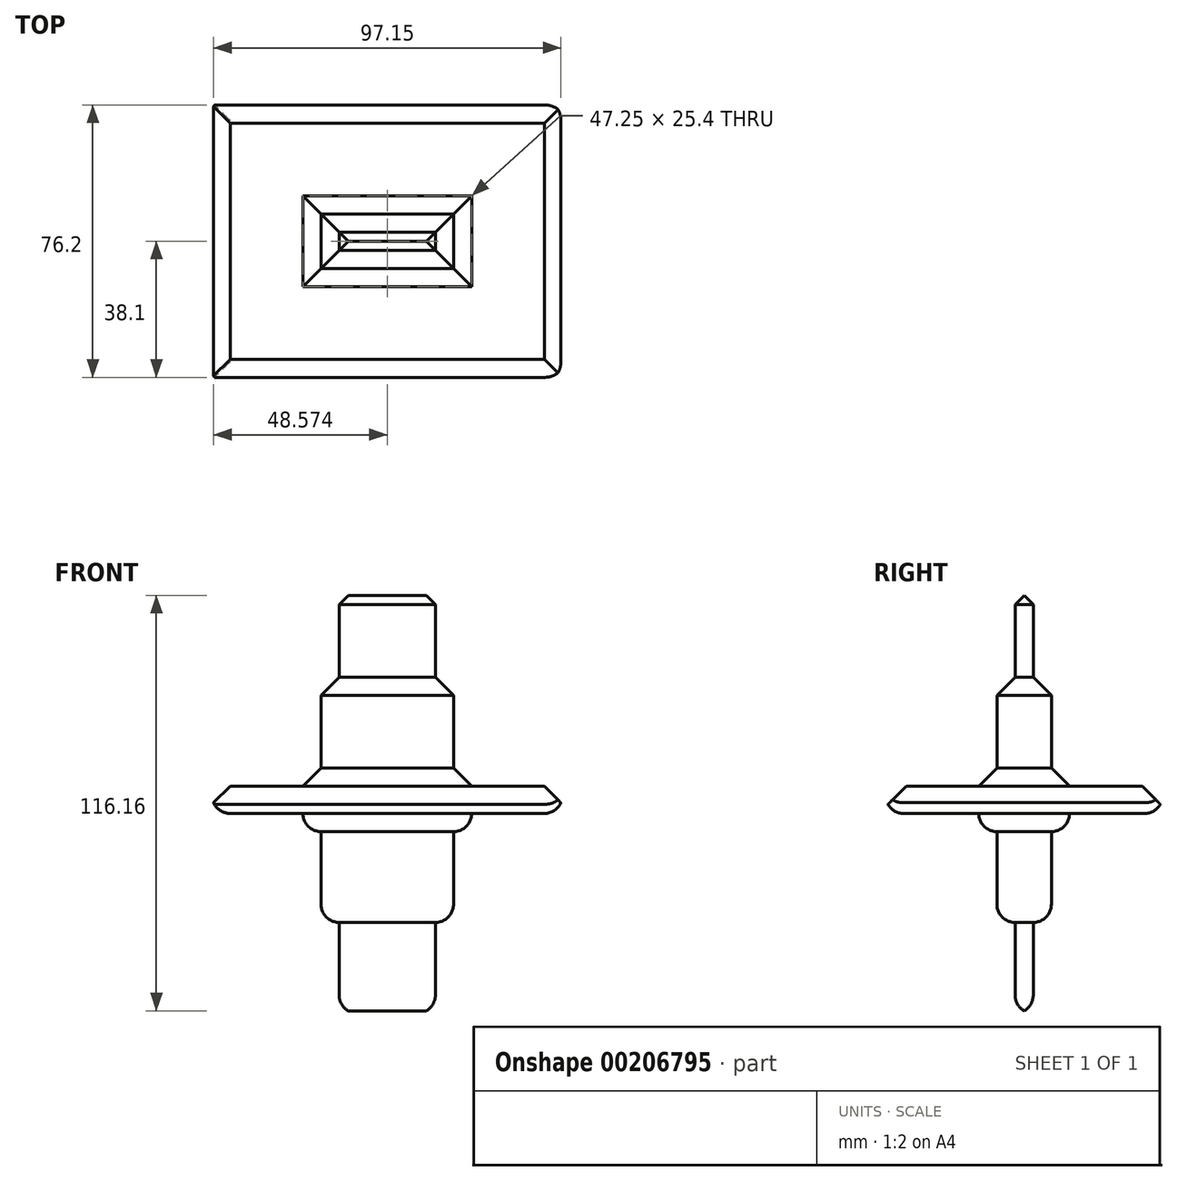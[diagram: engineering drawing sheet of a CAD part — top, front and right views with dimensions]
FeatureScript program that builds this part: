
annotation { "Feature Type Name" : "Feature", "Feature Type Description" : "" }
export const myFeature = defineFeature(function(context is Context, id is Id, definition is map)
    precondition{}
    {
        {
            var Q0;
            Q0=qCreatedBy(makeId("Front.planeOp"),FACE);
            var sketch = newSketch(context, id + "F0", { "sketchPlane" : qUnion([Q0])});
            skLineSegment(sketch, "E0", {"start": v(27.15, 7.6) * mm, "end": v(27.15, -10.17) * mm});
            skLineSegment(sketch, "E1", {"start": v(27.15, -10.17) * mm, "end": v(-20.1, -10.17) * mm});
            skLineSegment(sketch, "E2", {"start": v(-20.1, -10.17) * mm, "end": v(-20.1, 7.6) * mm});
            skLineSegment(sketch, "E3", {"start": v(-20.1, 7.6) * mm, "end": v(27.15, 7.6) * mm});
            skSolve(sketch);
        }
        {
            var Q0;
            Q0 = qSketchRegion(id + "F0", true);
            extrude(context, id + "F1", {"entities" : qUnion([Q0]), "depth" : 25.4 * mm});
        }
        {
            var Q0;
            Q0=makeQuery(id+"F1.opExtrude","SWEPT_FACE",FACE,{"disambiguationData":[OSD([sQuery(id+"F0.wireOp",EDGE,"E3")])]});
            chamfer(context, id + "F2", {"entities" : qUnion([Q0]), "width" : 5.08 * mm, "tangentPropagation" : true});
        }
        {
            var Q0;
            Q0=makeQuery(id+"F1.opExtrude","SWEPT_FACE",FACE,{"disambiguationData":[OSD([sQuery(id+"F0.wireOp",EDGE,"E1")])]});
            fillet(context, id + "F3", {"entities" : qUnion([Q0]), "radius" : 5.08 * mm, "tangentPropagation" : true, "allowEdgeOverflow" : false});
        }
        {
            var Q0;
            Q0=makeQuery(id+"F1.opExtrude","SWEPT_FACE",FACE,{"disambiguationData":[OSD([sQuery(id+"F0.wireOp",EDGE,"E1")])]});
            extrude(context, id + "F4", {"entities" : qUnion([Q0]), "operationType" : NewBodyOperationType.ADD, "depth" : 25.4 * mm});
        }
        {
            var Q0;
            Q0=makeQuery(id+"F4.opExtrude","CAP_FACE",FACE,{"disambiguationData":[OSD([sQuery(id+"F0.wireOp",EDGE,"E1")])],"isStart":false});
            fillet(context, id + "F5", {"entities" : qUnion([Q0]), "radius" : 5.08 * mm, "tangentPropagation" : true, "allowEdgeOverflow" : false});
        }
        {
            var Q0;
            Q0=makeQuery(id+"F4.opExtrude","CAP_FACE",FACE,{"disambiguationData":[OSD([sQuery(id+"F0.wireOp",EDGE,"E1")])],"isStart":false});
            extrude(context, id + "F6", {"entities" : qUnion([Q0]), "operationType" : NewBodyOperationType.ADD, "depth" : 25.4 * mm});
        }
        {
            var Q0;
            Q0=makeQuery(id+"F6.opExtrude","CAP_FACE",FACE,{"disambiguationData":[OSD([sQuery(id+"F0.wireOp",EDGE,"E1")])],"isStart":false});
            fillet(context, id + "F7", {"entities" : qUnion([Q0]), "radius" : 5.08 * mm, "tangentPropagation" : true, "allowEdgeOverflow" : false});
        }
        {
            var Q0;
            Q0=makeQuery(id+"F1.opExtrude","SWEPT_FACE",FACE,{"disambiguationData":[OSD([sQuery(id+"F0.wireOp",EDGE,"E3")])]});
            extrude(context, id + "F8", {"entities" : qUnion([Q0]), "operationType" : NewBodyOperationType.ADD, "depth" : 25.4 * mm});
        }
        {
            var Q0;
            Q0=makeQuery(id+"F8.opExtrude","CAP_FACE",FACE,{"disambiguationData":[OSD([sQuery(id+"F0.wireOp",EDGE,"E3")])],"isStart":false});
            chamfer(context, id + "F9", {"entities" : qUnion([Q0]), "width" : 5.08 * mm, "tangentPropagation" : true});
        }
        {
            var Q0;
            Q0=makeQuery(id+"F8.opExtrude","CAP_FACE",FACE,{"disambiguationData":[OSD([sQuery(id+"F0.wireOp",EDGE,"E3")])],"isStart":false});
            extrude(context, id + "F10", {"entities" : qUnion([Q0]), "operationType" : NewBodyOperationType.ADD, "depth" : 25.4 * mm});
        }
        {
            var Q0;
            Q0=makeQuery(id+"F10.opExtrude","CAP_FACE",FACE,{"disambiguationData":[OSD([sQuery(id+"F0.wireOp",EDGE,"E3")])],"isStart":false});
            chamfer(context, id + "F11", {"entities" : qUnion([Q0]), "width" : 5.08 * mm, "tangentPropagation" : true});
        }
        {
            var Q0;
            Q0=makeQuery(id+"F1.opExtrude","CAP_FACE",FACE,{"disambiguationData":[OSD([sQuery(id+"F0.wireOp",EDGE,"E0"),sQuery(id+"F0.wireOp",EDGE,"E1"),sQuery(id+"F0.wireOp",EDGE,"E2"),sQuery(id+"F0.wireOp",EDGE,"E3")])],"isStart":true});
            extrude(context, id + "F12", {"entities" : qUnion([Q0]), "operationType" : NewBodyOperationType.ADD, "depth" : 25.4 * mm});
        }
        {
            var Q0;
            {var subQ0=sQuery(id+"F0.wireOp",EDGE,"E3");var subQ1=sQuery(id+"F0.wireOp",EDGE,"E2");var subQ2=sQuery(id+"F0.wireOp",EDGE,"E1");var subQ3=sQuery(id+"F0.wireOp",EDGE,"E0");Q0=makeQuery(id+"F12.opExtrude","CAP_EDGE",EDGE,{"disambiguationData":[OSD([subQ3,subQ2,subQ1,subQ0]),TDD([makeQuery(id+"F2.opChamfer","BLEND_EDGE",EDGE,{"blendedFrom":[makeQuery(id+"F1.opExtrude","CAP_EDGE",EDGE,{"disambiguationData":[OSD([subQ0])],"isStart":true}),makeQuery(id+"F1.opExtrude","CAP_FACE",FACE,{"disambiguationData":[OSD([subQ3,subQ2,subQ1,subQ0])],"isStart":true})],"blendedInto":[makeQuery(id+"F1.opExtrude","CAP_FACE",FACE,{"disambiguationData":[OSD([subQ3,subQ2,subQ1,subQ0])],"isStart":true})]})])],"isStart":false});}
            chamfer(context, id + "F13", {"entities" : qUnion([Q0]), "width" : 5.08 * mm, "tangentPropagation" : true});
        }
        {
            var Q0;
            {var subQ0=sQuery(id+"F0.wireOp",EDGE,"E3");var subQ1=sQuery(id+"F0.wireOp",EDGE,"E2");var subQ2=sQuery(id+"F0.wireOp",EDGE,"E1");var subQ3=sQuery(id+"F0.wireOp",EDGE,"E0");Q0=makeQuery(id+"F12.opExtrude","CAP_EDGE",EDGE,{"disambiguationData":[OSD([subQ3,subQ2,subQ1,subQ0]),TDD([makeQuery(id+"F3.opFillet","BLEND_EDGE",EDGE,{"blendedFrom":[makeQuery(id+"F1.opExtrude","CAP_EDGE",EDGE,{"disambiguationData":[OSD([subQ2])],"isStart":true}),makeQuery(id+"F1.opExtrude","CAP_FACE",FACE,{"disambiguationData":[OSD([subQ3,subQ2,subQ1,subQ0])],"isStart":true})],"blendedInto":[makeQuery(id+"F1.opExtrude","CAP_FACE",FACE,{"disambiguationData":[OSD([subQ3,subQ2,subQ1,subQ0])],"isStart":true})]})])],"isStart":false});}
            fillet(context, id + "F14", {"entities" : qUnion([Q0]), "radius" : 5.08 * mm, "tangentPropagation" : true, "allowEdgeOverflow" : false});
        }
        {
            var Q0;
            Q0=makeQuery(id+"F1.opExtrude","CAP_FACE",FACE,{"disambiguationData":[OSD([sQuery(id+"F0.wireOp",EDGE,"E0"),sQuery(id+"F0.wireOp",EDGE,"E1"),sQuery(id+"F0.wireOp",EDGE,"E2"),sQuery(id+"F0.wireOp",EDGE,"E3")])],"isStart":false});
            extrude(context, id + "F15", {"entities" : qUnion([Q0]), "operationType" : NewBodyOperationType.ADD, "depth" : 25.4 * mm});
        }
        {
            var Q0;
            {var subQ0=sQuery(id+"F0.wireOp",EDGE,"E3");var subQ1=sQuery(id+"F0.wireOp",EDGE,"E2");var subQ2=sQuery(id+"F0.wireOp",EDGE,"E1");var subQ3=sQuery(id+"F0.wireOp",EDGE,"E0");Q0=makeQuery(id+"F15.opExtrude","CAP_EDGE",EDGE,{"disambiguationData":[OSD([subQ3,subQ2,subQ1,subQ0]),TDD([makeQuery(id+"F2.opChamfer","BLEND_EDGE",EDGE,{"blendedFrom":[makeQuery(id+"F1.opExtrude","CAP_EDGE",EDGE,{"disambiguationData":[OSD([subQ0])],"isStart":false}),makeQuery(id+"F1.opExtrude","CAP_FACE",FACE,{"disambiguationData":[OSD([subQ3,subQ2,subQ1,subQ0])],"isStart":false})],"blendedInto":[makeQuery(id+"F1.opExtrude","CAP_FACE",FACE,{"disambiguationData":[OSD([subQ3,subQ2,subQ1,subQ0])],"isStart":false})]})])],"isStart":false});}
            chamfer(context, id + "F16", {"entities" : qUnion([Q0]), "width" : 5.08 * mm, "tangentPropagation" : true});
        }
        {
            var Q0;
            {var subQ0=sQuery(id+"F0.wireOp",EDGE,"E3");var subQ1=sQuery(id+"F0.wireOp",EDGE,"E2");var subQ2=sQuery(id+"F0.wireOp",EDGE,"E1");var subQ3=sQuery(id+"F0.wireOp",EDGE,"E0");Q0=makeQuery(id+"F15.opExtrude","CAP_EDGE",EDGE,{"disambiguationData":[OSD([subQ3,subQ2,subQ1,subQ0]),TDD([makeQuery(id+"F3.opFillet","BLEND_EDGE",EDGE,{"blendedFrom":[makeQuery(id+"F1.opExtrude","CAP_EDGE",EDGE,{"disambiguationData":[OSD([subQ2])],"isStart":false}),makeQuery(id+"F1.opExtrude","CAP_FACE",FACE,{"disambiguationData":[OSD([subQ3,subQ2,subQ1,subQ0])],"isStart":false})],"blendedInto":[makeQuery(id+"F1.opExtrude","CAP_FACE",FACE,{"disambiguationData":[OSD([subQ3,subQ2,subQ1,subQ0])],"isStart":false})]})])],"isStart":false});}
            fillet(context, id + "F17", {"entities" : qUnion([Q0]), "radius" : 5.08 * mm, "tangentPropagation" : true, "allowEdgeOverflow" : false});
        }
        {
            var Q0;
            {var subQ0=sQuery(id+"F0.wireOp",EDGE,"E2");Q0=makeQuery(id+"F15.boolean.opBoolean","MERGE",FACE,{"derivedFrom":[makeQuery(id+"F12.boolean.opBoolean","MERGE",FACE,{"derivedFrom":[makeQuery(id+"F1.opExtrude","SWEPT_FACE",FACE,{"disambiguationData":[OSD([subQ0])]}),makeQuery(id+"F12.opExtrude","SWEPT_FACE",FACE,{"disambiguationData":[OSD([subQ0])]})]}),makeQuery(id+"F15.opExtrude","SWEPT_FACE",FACE,{"disambiguationData":[OSD([subQ0])]})]});}
            extrude(context, id + "F18", {"entities" : qUnion([Q0]), "operationType" : NewBodyOperationType.ADD, "depth" : 25.4 * mm});
        }
        {
            var Q0;
            {var subQ0=sQuery(id+"F0.wireOp",EDGE,"E2");var subQ1=makeQuery(id+"F1.opExtrude","SWEPT_FACE",FACE,{"disambiguationData":[OSD([subQ0])]});var subQ2=sQuery(id+"F0.wireOp",EDGE,"E3");var subQ3=sQuery(id+"F0.wireOp",EDGE,"E1");var subQ4=sQuery(id+"F0.wireOp",EDGE,"E0");var subQ5=makeQuery(id+"F1.opExtrude","SWEPT_EDGE",EDGE,{"disambiguationData":[OSD([subQ3,subQ0])]});Q0=makeQuery(id+"F18.opExtrude","CAP_EDGE",EDGE,{"disambiguationData":[OSD([subQ4,subQ3,subQ0,subQ2]),TDD([makeQuery(id+"F3.opFillet","BLEND_EDGE",EDGE,{"blendedFrom":[subQ5,subQ1],"blendedInto":[subQ1]}),makeQuery(id+"F12.opExtrude","SWEPT_EDGE",EDGE,{"disambiguationData":[OSD([subQ4,subQ3,subQ0,subQ2]),TDD([makeQuery(id+"F3.opFillet","BLEND_VERTEX",VERTEX,{"blendedFrom":[subQ5,makeQuery(id+"F1.opExtrude","CAP_EDGE",EDGE,{"disambiguationData":[OSD([subQ3])],"isStart":true}),makeQuery(id+"F1.opExtrude","CAP_FACE",FACE,{"disambiguationData":[OSD([subQ4,subQ3,subQ0,subQ2])],"isStart":true}),subQ1],"blendedInto":[makeQuery(id+"F1.opExtrude","CAP_FACE",FACE,{"disambiguationData":[OSD([subQ4,subQ3,subQ0,subQ2])],"isStart":true}),subQ1]})])]}),makeQuery(id+"F15.opExtrude","SWEPT_EDGE",EDGE,{"disambiguationData":[OSD([subQ4,subQ3,subQ0,subQ2]),TDD([makeQuery(id+"F3.opFillet","BLEND_VERTEX",VERTEX,{"blendedFrom":[subQ5,makeQuery(id+"F1.opExtrude","CAP_EDGE",EDGE,{"disambiguationData":[OSD([subQ3])],"isStart":false}),makeQuery(id+"F1.opExtrude","CAP_FACE",FACE,{"disambiguationData":[OSD([subQ4,subQ3,subQ0,subQ2])],"isStart":false}),subQ1],"blendedInto":[makeQuery(id+"F1.opExtrude","CAP_FACE",FACE,{"disambiguationData":[OSD([subQ4,subQ3,subQ0,subQ2])],"isStart":false}),subQ1]})])]})])],"isStart":false});}
            fillet(context, id + "F19", {"entities" : qUnion([Q0]), "radius" : 5.08 * mm, "tangentPropagation" : true, "allowEdgeOverflow" : false});
        }
        {
            var Q0;
            {var subQ0=sQuery(id+"F0.wireOp",EDGE,"E2");var subQ1=makeQuery(id+"F1.opExtrude","SWEPT_FACE",FACE,{"disambiguationData":[OSD([subQ0])]});var subQ2=sQuery(id+"F0.wireOp",EDGE,"E3");var subQ3=sQuery(id+"F0.wireOp",EDGE,"E1");var subQ4=sQuery(id+"F0.wireOp",EDGE,"E0");var subQ5=makeQuery(id+"F1.opExtrude","SWEPT_EDGE",EDGE,{"disambiguationData":[OSD([subQ0,subQ2])]});Q0=makeQuery(id+"F18.opExtrude","CAP_EDGE",EDGE,{"disambiguationData":[OSD([subQ4,subQ3,subQ0,subQ2]),TDD([makeQuery(id+"F2.opChamfer","BLEND_EDGE",EDGE,{"blendedFrom":[subQ5,subQ1],"blendedInto":[subQ1]}),makeQuery(id+"F12.opExtrude","SWEPT_EDGE",EDGE,{"disambiguationData":[OSD([subQ4,subQ3,subQ0,subQ2]),TDD([makeQuery(id+"F2.opChamfer","BLEND_VERTEX",VERTEX,{"blendedFrom":[subQ5,makeQuery(id+"F1.opExtrude","CAP_EDGE",EDGE,{"disambiguationData":[OSD([subQ2])],"isStart":true}),makeQuery(id+"F1.opExtrude","CAP_FACE",FACE,{"disambiguationData":[OSD([subQ4,subQ3,subQ0,subQ2])],"isStart":true}),subQ1],"blendedInto":[makeQuery(id+"F1.opExtrude","CAP_FACE",FACE,{"disambiguationData":[OSD([subQ4,subQ3,subQ0,subQ2])],"isStart":true}),subQ1]})])]}),makeQuery(id+"F15.opExtrude","SWEPT_EDGE",EDGE,{"disambiguationData":[OSD([subQ4,subQ3,subQ0,subQ2]),TDD([makeQuery(id+"F2.opChamfer","BLEND_VERTEX",VERTEX,{"blendedFrom":[subQ5,makeQuery(id+"F1.opExtrude","CAP_EDGE",EDGE,{"disambiguationData":[OSD([subQ2])],"isStart":false}),makeQuery(id+"F1.opExtrude","CAP_FACE",FACE,{"disambiguationData":[OSD([subQ4,subQ3,subQ0,subQ2])],"isStart":false}),subQ1],"blendedInto":[makeQuery(id+"F1.opExtrude","CAP_FACE",FACE,{"disambiguationData":[OSD([subQ4,subQ3,subQ0,subQ2])],"isStart":false}),subQ1]})])]})])],"isStart":false});}
            chamfer(context, id + "F20", {"entities" : qUnion([Q0]), "width" : 5.08 * mm, "tangentPropagation" : true});
        }
        {
            var Q0;
            {var subQ0=sQuery(id+"F0.wireOp",EDGE,"E0");Q0=makeQuery(id+"F15.boolean.opBoolean","MERGE",FACE,{"derivedFrom":[makeQuery(id+"F12.boolean.opBoolean","MERGE",FACE,{"derivedFrom":[makeQuery(id+"F1.opExtrude","SWEPT_FACE",FACE,{"disambiguationData":[OSD([subQ0])]}),makeQuery(id+"F12.opExtrude","SWEPT_FACE",FACE,{"disambiguationData":[OSD([subQ0])]})]}),makeQuery(id+"F15.opExtrude","SWEPT_FACE",FACE,{"disambiguationData":[OSD([subQ0])]})]});}
            extrude(context, id + "F21", {"entities" : qUnion([Q0]), "operationType" : NewBodyOperationType.ADD, "depth" : 25.4 * mm});
        }
        {
            var Q0;
            {var subQ0=sQuery(id+"F0.wireOp",EDGE,"E3");var subQ1=sQuery(id+"F0.wireOp",EDGE,"E2");var subQ2=sQuery(id+"F0.wireOp",EDGE,"E1");var subQ3=sQuery(id+"F0.wireOp",EDGE,"E0");var subQ4=makeQuery(id+"F1.opExtrude","SWEPT_FACE",FACE,{"disambiguationData":[OSD([subQ3])]});var subQ5=makeQuery(id+"F1.opExtrude","SWEPT_EDGE",EDGE,{"disambiguationData":[OSD([subQ3,subQ0])]});Q0=makeQuery(id+"F21.opExtrude","CAP_EDGE",EDGE,{"disambiguationData":[OSD([subQ3,subQ2,subQ1,subQ0]),TDD([makeQuery(id+"F2.opChamfer","BLEND_EDGE",EDGE,{"blendedFrom":[subQ5,subQ4],"blendedInto":[subQ4]}),makeQuery(id+"F12.opExtrude","SWEPT_EDGE",EDGE,{"disambiguationData":[OSD([subQ3,subQ2,subQ1,subQ0]),TDD([makeQuery(id+"F2.opChamfer","BLEND_VERTEX",VERTEX,{"blendedFrom":[subQ5,makeQuery(id+"F1.opExtrude","CAP_EDGE",EDGE,{"disambiguationData":[OSD([subQ0])],"isStart":true}),subQ4,makeQuery(id+"F1.opExtrude","CAP_FACE",FACE,{"disambiguationData":[OSD([subQ3,subQ2,subQ1,subQ0])],"isStart":true})],"blendedInto":[subQ4,makeQuery(id+"F1.opExtrude","CAP_FACE",FACE,{"disambiguationData":[OSD([subQ3,subQ2,subQ1,subQ0])],"isStart":true})]})])]}),makeQuery(id+"F15.opExtrude","SWEPT_EDGE",EDGE,{"disambiguationData":[OSD([subQ3,subQ2,subQ1,subQ0]),TDD([makeQuery(id+"F2.opChamfer","BLEND_VERTEX",VERTEX,{"blendedFrom":[subQ5,makeQuery(id+"F1.opExtrude","CAP_EDGE",EDGE,{"disambiguationData":[OSD([subQ0])],"isStart":false}),subQ4,makeQuery(id+"F1.opExtrude","CAP_FACE",FACE,{"disambiguationData":[OSD([subQ3,subQ2,subQ1,subQ0])],"isStart":false})],"blendedInto":[subQ4,makeQuery(id+"F1.opExtrude","CAP_FACE",FACE,{"disambiguationData":[OSD([subQ3,subQ2,subQ1,subQ0])],"isStart":false})]})])]})])],"isStart":false});}
            chamfer(context, id + "F22", {"entities" : qUnion([Q0]), "width" : 5.08 * mm, "tangentPropagation" : true});
        }
        {
            var Q0;
            {var subQ0=sQuery(id+"F0.wireOp",EDGE,"E3");var subQ1=sQuery(id+"F0.wireOp",EDGE,"E2");var subQ2=sQuery(id+"F0.wireOp",EDGE,"E1");var subQ3=sQuery(id+"F0.wireOp",EDGE,"E0");var subQ4=makeQuery(id+"F1.opExtrude","SWEPT_FACE",FACE,{"disambiguationData":[OSD([subQ3])]});var subQ5=makeQuery(id+"F1.opExtrude","SWEPT_EDGE",EDGE,{"disambiguationData":[OSD([subQ3,subQ2])]});Q0=makeQuery(id+"F21.opExtrude","CAP_EDGE",EDGE,{"disambiguationData":[OSD([subQ3,subQ2,subQ1,subQ0]),TDD([makeQuery(id+"F3.opFillet","BLEND_EDGE",EDGE,{"blendedFrom":[subQ5,subQ4],"blendedInto":[subQ4]}),makeQuery(id+"F12.opExtrude","SWEPT_EDGE",EDGE,{"disambiguationData":[OSD([subQ3,subQ2,subQ1,subQ0]),TDD([makeQuery(id+"F3.opFillet","BLEND_VERTEX",VERTEX,{"blendedFrom":[subQ5,makeQuery(id+"F1.opExtrude","CAP_EDGE",EDGE,{"disambiguationData":[OSD([subQ2])],"isStart":true}),subQ4,makeQuery(id+"F1.opExtrude","CAP_FACE",FACE,{"disambiguationData":[OSD([subQ3,subQ2,subQ1,subQ0])],"isStart":true})],"blendedInto":[subQ4,makeQuery(id+"F1.opExtrude","CAP_FACE",FACE,{"disambiguationData":[OSD([subQ3,subQ2,subQ1,subQ0])],"isStart":true})]})])]}),makeQuery(id+"F15.opExtrude","SWEPT_EDGE",EDGE,{"disambiguationData":[OSD([subQ3,subQ2,subQ1,subQ0]),TDD([makeQuery(id+"F3.opFillet","BLEND_VERTEX",VERTEX,{"blendedFrom":[subQ5,makeQuery(id+"F1.opExtrude","CAP_EDGE",EDGE,{"disambiguationData":[OSD([subQ2])],"isStart":false}),subQ4,makeQuery(id+"F1.opExtrude","CAP_FACE",FACE,{"disambiguationData":[OSD([subQ3,subQ2,subQ1,subQ0])],"isStart":false})],"blendedInto":[subQ4,makeQuery(id+"F1.opExtrude","CAP_FACE",FACE,{"disambiguationData":[OSD([subQ3,subQ2,subQ1,subQ0])],"isStart":false})]})])]})])],"isStart":false});}
            fillet(context, id + "F23", {"entities" : qUnion([Q0]), "radius" : 5.08 * mm, "tangentPropagation" : true, "allowEdgeOverflow" : false});
        }
    });
